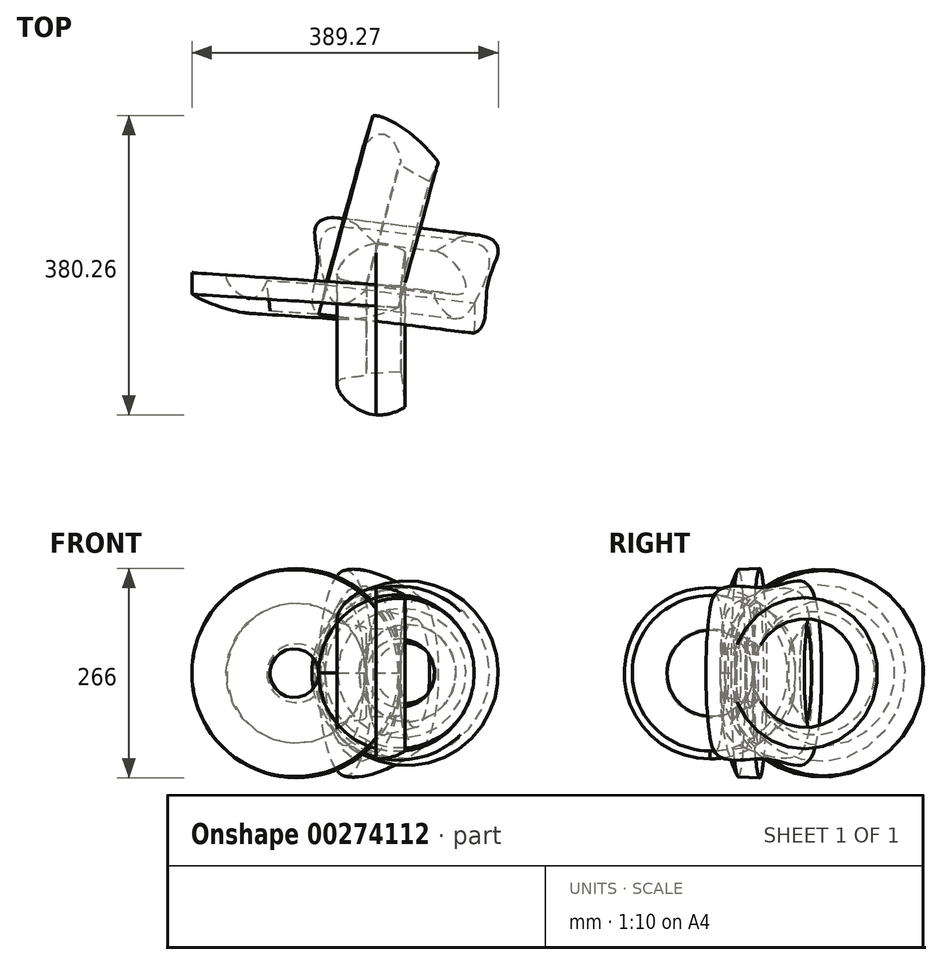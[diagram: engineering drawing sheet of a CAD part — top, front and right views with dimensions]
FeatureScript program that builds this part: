
annotation { "Feature Type Name" : "Feature", "Feature Type Description" : "" }
export const myFeature = defineFeature(function(context is Context, id is Id, definition is map)
    precondition{}
    {
        {
            var Q0;
            Q0=qCreatedBy(makeId("Top.planeOp"),FACE);
            var sketch = newSketch(context, id + "F0", { "sketchPlane" : qUnion([Q0])});
            skFitSpline(sketch, "E0", {"points": [v(-45.83, 16.01) * mm, v(-44.02, -46.79) * mm, v(89.73, -12.37) * mm, v(28.44, 42.88) * mm, v(-18.96, 0) * mm, v(16.36, -9.65) * mm, v(-13.53, -34.1) * mm, v(-35.27, -9.35) * mm, v(-32.25, 61) * mm, v(7, 63.11) * mm, v(-14.43, 74.58) * mm, v(-47.04, 66.73) * mm, v(-45.83, 16.01) * mm]});
            skLineSegment(sketch, "E1", {"start": v(7, 63.11) * mm, "end": v(28.44, 42.88) * mm});
            skLineSegment(sketch, "E2", {"start": v(16.36, -9.65) * mm, "end": v(89.73, -12.37) * mm});
            skLineSegment(sketch, "E3", {"start": v(-35.27, -9.35) * mm, "end": v(-44.02, -46.79) * mm});
            skLineSegment(sketch, "E4", {"start": v(39, 66.13) * mm, "end": v(68.9, 57.98) * mm});
            skLineSegment(sketch, "E5", {"start": v(68.9, 57.98) * mm, "end": v(53.8, -65.8) * mm});
            skLineSegment(sketch, "E6", {"start": v(53.8, -65.8) * mm, "end": v(-44.02, -65.8) * mm});
            skLineSegment(sketch, "E7", {"start": v(-44.02, -65.8) * mm, "end": v(-72.1, 0) * mm});
            skLineSegment(sketch, "E8", {"start": v(-72.1, 0) * mm, "end": v(-69.08, 46.2) * mm});
            skSolve(sketch);
        }
        {
            var Q0;
            {var subQ0=sQuery(id+"F0.wireOp",EDGE,"E0");var subQ1=makeQuery(id+"F0.imprint","INTERSECT",VERTEX,{"disambiguationData":[OD(1.0)],"derivedFrom":[subQ0,sQuery(id+"F0.wireOp",EDGE,"E1")]});Q0=makeQuery(id+"F0.imprint","IMPRINT",FACE,{"disambiguationData":[TD([[makeQuery(id+"F0.imprint","IMPRINT",EDGE,{"disambiguationData":[TD([[subQ1,1.0]])],"derivedFrom":subQ0}),1.0]])]});}
            var Q1;
            Q1=sQuery(id+"F0.wireOp",EDGE,"E6");
            revolve(context, id + "F1", {"entities" : qUnion([Q0]), "axis" : qUnion([Q1]), "revolveType" : RevolveType.FULL});
        }
        {
            var Q0;
            {var subQ2=sQuery(id+"F0.wireOp",EDGE,"E3");Q0=makeQuery(id+"F0.imprint","IMPRINT",FACE,{"disambiguationData":[TD([[makeQuery(id+"F0.imprint","IMPRINT",EDGE,{"derivedFrom":subQ2}),-1.0]])]});}
            var Q1;
            Q1=sQuery(id+"F0.wireOp",EDGE,"E5");
            revolve(context, id + "F2", {"entities" : qUnion([Q0]), "axis" : qUnion([Q1]), "revolveType" : RevolveType.FULL});
        }
        {
            var Q0;
            {var subQ0=sQuery(id+"F0.wireOp",EDGE,"E3");Q0=makeQuery(id+"F0.imprint","IMPRINT",FACE,{"disambiguationData":[TD([[makeQuery(id+"F0.imprint","IMPRINT",EDGE,{"derivedFrom":subQ0}),1.0]])]});}
            var Q1;
            Q1=sQuery(id+"F0.wireOp",EDGE,"E8");
            revolve(context, id + "F3", {"entities" : qUnion([Q0]), "axis" : qUnion([Q1]), "revolveType" : RevolveType.FULL});
        }
        {
            var Q0;
            {var subQ0=sQuery(id+"F0.wireOp",EDGE,"E3");Q0=makeQuery(id+"F0.imprint","IMPRINT",FACE,{"disambiguationData":[TD([[makeQuery(id+"F0.imprint","IMPRINT",EDGE,{"derivedFrom":subQ0}),1.0]])]});}
            var Q1;
            Q1=sQuery(id+"F0.wireOp",EDGE,"E4");
            revolve(context, id + "F4", {"entities" : qUnion([Q0]), "axis" : qUnion([Q1]), "revolveType" : RevolveType.FULL});
        }
        {
            var Q0;
            {var subQ0=sQuery(id+"F0.wireOp",EDGE,"E1");Q0=makeQuery(id+"F0.imprint","IMPRINT",FACE,{"disambiguationData":[TD([[makeQuery(id+"F0.imprint","IMPRINT",EDGE,{"derivedFrom":subQ0}),-1.0]])]});}
            var Q1;
            Q1=sQuery(id+"F0.wireOp",EDGE,"E5");
            revolve(context, id + "F5", {"entities" : qUnion([Q0]), "axis" : qUnion([Q1]), "revolveType" : RevolveType.FULL});
        }
    });
